# Revit family: Door-NanaWall-ClimaCLEAR_Concept_1
name_source: partatom
category: Doors
units: mm (PartAtom-declared; Revit-internal decimal feet)

## family parameters
Always vertical = Yes
Classification Number = 23.30.10.17.11
Cut with Voids When Loaded = No
Host = Wall
Room Calculation Point = No
Shared = No

## types (1)
- Standard
    04 CSI = 08 41 13
    95 CSI = 8411
    Analytic Construction = <None>
    Assembly Code = B2030110
    Cost = 0 $
    Cost Info = https://www.nanawall.com
    Description = Frameless all glass individual panel sliding system
    Detail Component in Plan = Yes
    Detail Component in Section = Yes
    Engineering Details URL = https://www.nanawall.com
    Exterior Wall Offset = 2"
    Glass Material = Glass - NanaWall - Generic
    Glazing Options = https://www.nanawall.com
    Green Building-LEED = https://www.arcat.com
    Height = 9' - 0"
    Height Constraint = 9' - 0"
    Installation and Service URL = https://www.nanawall.com
    Jamb Height = 9' - 0 61/64"
    Keynote = 08 41 00
    Manufacturer = NanaWall Systems, Inc.
    Manufacturer Fax = (415) 383-0312
    Manufacturer Website = https://www.nanawall.com
    Max Panel Height = 9' - 0"
    Model = ClimaCLEAR - Concept 1
    NanaWall Configurator = http://www.nanawall.com
    Opening Width = 9' - 8 9/64"
    Panel Height = 9' - 0"
    Performance URL = https://www.nanawall.com
    Product Data = https://www.arcat.com
    Product Page URL = https://www.nanawall.com
    Rough Height = 9' - 0"
    Rough Width = 9' - 10 7/64"
    Sales Information = https://www.nanawall.com
    Sash = Metal - NanaWall - Aluminum
    Sills Available = Raised, Low Profile Saddle, Flush
    Size Note = Adjust Height and Width as necessary to fit your project needs. Multiple Panel and opening configurations are available. See Product Page URL for more information.
    Specification = https://www.arcat.com
    Subcategory = Folding Door
    Thickness = 2 1/2"
    URL = http://www.nanawall.com
    Wall Closure = By host
    Warranty URL = http://www.nanawall.com
    Width = 10' - 0"

## geometry (parser evidence)
native form markers: Blend x4, Sweep x19
no freeform markers — native parametric forms only
